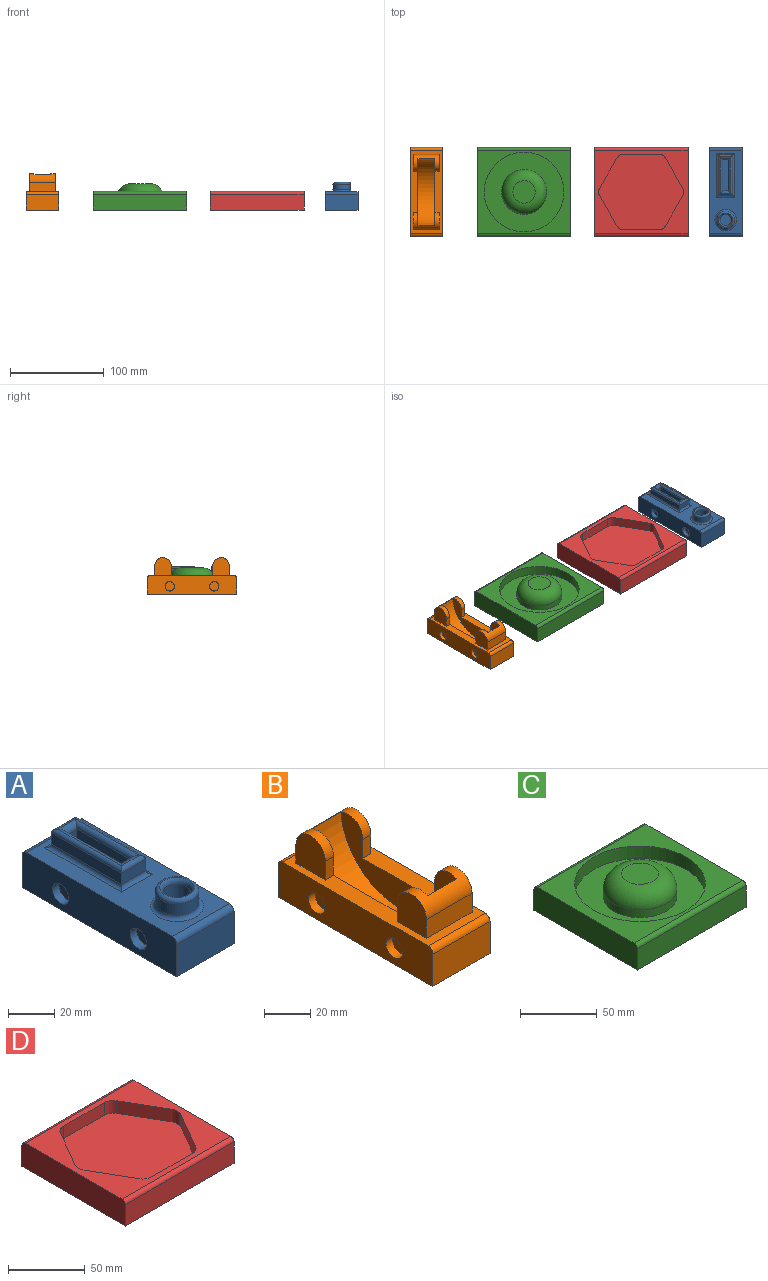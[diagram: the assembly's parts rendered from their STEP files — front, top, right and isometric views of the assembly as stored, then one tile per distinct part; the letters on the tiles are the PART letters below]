
ASSEMBLY  parts=4 mates=3
PART A: 43 faces, bbox 35x95x30.4 mm
  f0: plane 95x20mm, normal (-1,0,0), area 1732.7mm2, adj f2,f3,f4,f5,f18,f19,f39,f41
  f1: plane 95x20mm, normal (1,0,0), area 1732.7mm2, adj f2,f3,f4,f5,f18,f19,f35,f37
  f2: plane 89x35mm, normal (0,0,1), area 1806.5mm2, adj f0,f1,f18,f19,f30,f31,f32,f33
  f3: plane 35x17mm, normal (0,-1,0), area 595mm2, adj f0,f1,f5,f18
  f4: plane 35x17mm, normal (0,1,0), area 595mm2, adj f0,f1,f5,f19
  f5: plane 95x35mm, normal (0,0,-1), area 3325mm2, adj f0,f1,f3,f4
  f6: plane 33.08x17.5mm, normal (-1,0,0), area 577.5mm2, adj f7,f13,f17,f26,f28,f29
  f7: plane 17x6mm, normal (0,1,0), area 102mm2, adj f6,f8,f17,f28
  f8: plane 33.08x17.5mm, normal (1,0,0), area 577.5mm2, adj f7,f13,f17,f25,f28,f29
  f9: plane 15x6mm, normal (0,-1,0), area 90mm2, adj f10,f12,f23,f33
  f10: plane 43x6mm, normal (1,0,0), area 258mm2, adj f9,f11,f24,f34
  f11: plane 15x6mm, normal (0,1,0), area 90mm2, adj f10,f12,f22,f32
  f12: plane 43x6mm, normal (-1,0,0), area 258mm2, adj f9,f11,f21,f31
  f13: plane 17x6mm, normal (0,-1,0), area 102mm2, adj f6,f8,f17,f29
  f14: cylinder r=6mm len=17.4mm, axis (0,0,-1), area 656mm2, adj f16,f27
  f15: cylinder r=9.5mm len=19mm, axis (0,0,-1), area 358.1mm2, adj f20,f30
  f16: plane 12x12mm, normal (0,0,1), area 113.1mm2, adj f14
  f17: plane 33x6mm, normal (0,0,1), area 198mm2, adj f6,f7,f8,f13
  f18: cylinder r=3mm len=35mm, axis (-1,0,0), area 164.9mm2, adj f0,f1,f2,f3
  f19: cylinder r=3mm len=35mm, axis (1,0,0), area 164.9mm2, adj f0,f1,f2,f4
  f20: torus R=7.5mm, axis (0,0,1), area 173.2mm2, adj f15,f27
  f21: cylinder r=2mm len=43mm, axis (0,1,0), area 130.5mm2, adj f12,f22,f23,f25
  f22: cylinder r=2mm len=15mm, axis (1,0,0), area 42.6mm2, adj f11,f21,f24,f29
  f23: cylinder r=2mm len=15mm, axis (-1,0,0), area 42.6mm2, adj f9,f21,f24,f28
  f24: cylinder r=2mm len=43mm, axis (0,-1,0), area 130.5mm2, adj f10,f22,f23,f26
  f25: cylinder r=2.5mm len=39mm, axis (0,-1,0), area 139mm2, adj f8,f21,f28,f29
  f26: cylinder r=2.5mm len=39mm, axis (0,1,0), area 139mm2, adj f6,f24,f28,f29
  f27: torus R=9mm, axis (0,0,1), area 128.7mm2, adj f14,f20
  f28: cylinder r=3mm len=11mm, axis (1,0,0), area 36mm2, adj f6,f7,f8,f23,f25,f26
  f29: cylinder r=3mm len=11mm, axis (-1,0,0), area 36mm2, adj f6,f8,f13,f22,f25,f26
  f30: torus R=11.5mm, axis (0,0,1), area 201.9mm2, adj f2,f15
  f31: cylinder r=2mm len=47mm, axis (0,-1,0), area 139.7mm2, adj f2,f12,f32,f33
  f32: cylinder r=2mm len=19mm, axis (-1,0,0), area 51.7mm2, adj f2,f11,f31,f34
  f33: cylinder r=2mm len=19mm, axis (1,0,0), area 51.7mm2, adj f2,f9,f31,f34
  f34: cylinder r=2mm len=47mm, axis (0,1,0), area 139.7mm2, adj f2,f10,f32,f33
  f35: cylinder r=5.1mm len=10.2mm, axis (1,0,0), area 131.4mm2, adj f1,f36
  f36: plane 10.2x10.2mm, normal (1,0,0), area 81.7mm2, adj f35
  f37: cylinder r=5.1mm len=10.2mm, axis (1,0,0), area 131.4mm2, adj f1,f38
  f38: plane 10.2x10.2mm, normal (1,0,0), area 81.7mm2, adj f37
  f39: cylinder r=5.1mm len=10.2mm, axis (-1,0,0), area 131.4mm2, adj f0,f40
  f40: plane 10.2x10.2mm, normal (-1,0,0), area 81.7mm2, adj f39
  f41: cylinder r=5.1mm len=10.2mm, axis (-1,0,0), area 131.4mm2, adj f0,f42
  f42: plane 10.2x10.2mm, normal (-1,0,0), area 81.7mm2, adj f41
PART B: 31 faces, bbox 35x95x39 mm
  f0: plane 95x20mm, normal (-1,0,0), area 1735.9mm2, adj f2,f7,f8,f9,f21,f22,f27,f29
  f1: plane 95x20mm, normal (1,0,0), area 1735.9mm2, adj f2,f7,f8,f9,f21,f22,f23,f25
  f2: plane 89x35mm, normal (0,0,1), area 1315mm2, adj f0,f1,f3,f4,f10,f11,f12,f13
  f3: plane 10x5mm, normal (0,-1,0), area 50mm2, adj f2,f5,f11,f19
  f4: plane 10x5mm, normal (0,1,0), area 50mm2, adj f2,f6,f16,f19
  f5: cylinder r=9mm len=28mm, axis (1,0,0), area 454.4mm2, adj f3,f10,f11,f12,f13,f18,f19,f20
  f6: cylinder r=9mm len=28mm, axis (1,0,0), area 454.4mm2, adj f4,f14,f15,f16,f17,f18,f19,f20
  f7: plane 35x17mm, normal (0,-1,0), area 595mm2, adj f0,f1,f9,f22
  f8: plane 35x17mm, normal (0,1,0), area 595mm2, adj f0,f1,f9,f21
  f9: plane 95x35mm, normal (0,0,-1), area 3325mm2, adj f0,f1,f7,f8
  f10: plane 28x10mm, normal (0,1,0), area 280mm2, adj f2,f5,f11,f13
  f11: plane 19x18mm, normal (-1,0,0), area 307.2mm2, adj f2,f3,f5,f10
  f12: plane 10x5mm, normal (0,-1,0), area 50mm2, adj f2,f5,f13,f20
  f13: plane 19x18mm, normal (1,0,0), area 307.2mm2, adj f2,f5,f10,f12
  f14: plane 19x18mm, normal (1,0,0), area 307.2mm2, adj f2,f6,f15,f17
  f15: plane 10x5mm, normal (0,1,0), area 50mm2, adj f2,f6,f14,f20
  f16: plane 19x18mm, normal (-1,0,0), area 307.2mm2, adj f2,f4,f6,f17
  f17: plane 28x10mm, normal (0,-1,0), area 280mm2, adj f2,f6,f14,f16
  f18: cylinder r=35.5mm len=70.8mm, axis (1,0,0), area 1912mm2, adj f5,f6,f19,f20
  f19: plane 70.8x34mm, normal (1,0,0), area 999mm2, adj f2,f3,f4,f5,f6,f18
  f20: plane 70.8x34mm, normal (-1,0,0), area 999mm2, adj f2,f5,f6,f12,f15,f18
  f21: cylinder r=3mm len=35mm, axis (1,0,0), area 164.9mm2, adj f0,f1,f2,f8
  f22: cylinder r=3mm len=35mm, axis (-1,0,0), area 164.9mm2, adj f0,f1,f2,f7
  f23: cylinder r=5.05mm len=10.1mm, axis (1,0,0), area 130.1mm2, adj f1,f24
  f24: plane 10.1x10.1mm, normal (1,0,0), area 80.1mm2, adj f23
  f25: cylinder r=5.05mm len=10.1mm, axis (1,0,0), area 130.1mm2, adj f1,f26
  f26: plane 10.1x10.1mm, normal (1,0,0), area 80.1mm2, adj f25
  f27: cylinder r=5.05mm len=10.1mm, axis (-1,0,0), area 130.1mm2, adj f0,f28
  f28: plane 10.1x10.1mm, normal (-1,0,0), area 80.1mm2, adj f27
  f29: cylinder r=5.05mm len=10.1mm, axis (-1,0,0), area 130.1mm2, adj f0,f30
  f30: plane 10.1x10.1mm, normal (-1,0,0), area 80.1mm2, adj f29
PART C: 13 faces, bbox 100x95x28 mm
  f0: plane 95x20mm, normal (-1,0,0), area 1896.1mm2, adj f1,f3,f4,f5,f11,f12
  f1: plane 100x17mm, normal (0,-1,0), area 1700mm2, adj f0,f2,f5,f11
  f2: plane 95x20mm, normal (1,0,0), area 1896.1mm2, adj f1,f3,f4,f5,f11,f12
  f3: plane 100x17mm, normal (0,1,0), area 1700mm2, adj f0,f2,f5,f12
  f4: plane 100x89mm, normal (0,0,1), area 3225.5mm2, adj f0,f2,f7,f11,f12
  f5: plane 100x95mm, normal (0,0,-1), area 9500mm2, adj f0,f1,f2,f3
  f6: cylinder r=24mm len=48mm, axis (0,0,1), area 904.8mm2, adj f8,f10
  f7: cylinder r=42.5mm len=85mm, axis (0,0,1), area 2670.4mm2, adj f4,f8
  f8: plane 85x85mm, normal (0,0,1), area 3864.9mm2, adj f6,f7
  f9: plane 24x24mm, normal (0,0,1), area 452.4mm2, adj f10
  f10: torus R=12mm, axis (0,0,1), area 2326mm2, adj f6,f9
  f11: cylinder r=3mm len=100mm, axis (-1,0,0), area 471.2mm2, adj f0,f1,f2,f4
  f12: cylinder r=3mm len=100mm, axis (1,0,0), area 471.2mm2, adj f0,f2,f3,f4
PART D: 21 faces, bbox 100x95x20 mm
  f0: plane 100x89mm, normal (0,0,1), area 3238.6mm2, adj f2,f4,f6,f7,f8,f9,f10,f11
  f1: plane 100x17mm, normal (0,-1,0), area 1700mm2, adj f2,f4,f5,f20
  f2: plane 95x20mm, normal (1,0,0), area 1896.1mm2, adj f0,f1,f3,f5,f19,f20
  f3: plane 100x17mm, normal (0,1,0), area 1700mm2, adj f2,f4,f5,f19
  f4: plane 95x20mm, normal (-1,0,0), area 1896.1mm2, adj f0,f1,f3,f5,f19,f20
  f5: plane 100x95mm, normal (0,0,-1), area 9500mm2, adj f1,f2,f3,f4
  f6: cylinder r=8mm len=10mm, axis (0,0,1), area 83.8mm2, adj f0,f7,f17,f18
  f7: plane 32.5x18.76mm, normal (-0.87,-0.5,0), area 375.3mm2, adj f0,f6,f8,f18
  f8: cylinder r=8mm len=10mm, axis (0,0,1), area 83.8mm2, adj f0,f7,f9,f18
  f9: plane 37.53x10mm, normal (0,-1,0), area 375.3mm2, adj f0,f8,f10,f18
  f10: cylinder r=8mm len=10mm, axis (0,0,1), area 83.8mm2, adj f0,f9,f11,f18
  f11: plane 32.5x18.76mm, normal (0.87,-0.5,0), area 375.3mm2, adj f0,f10,f12,f18
  f12: cylinder r=8mm len=10mm, axis (0,0,1), area 83.8mm2, adj f0,f11,f13,f18
  f13: plane 32.5x18.76mm, normal (0.87,0.5,0), area 375.3mm2, adj f0,f12,f14,f18
  f14: cylinder r=8mm len=10mm, axis (0,0,1), area 83.8mm2, adj f0,f13,f15,f18
  f15: plane 37.53x10mm, normal (0,1,0), area 375.3mm2, adj f0,f14,f16,f18
  f16: cylinder r=8mm len=10mm, axis (0,0,1), area 83.8mm2, adj f0,f15,f17,f18
  f17: plane 32.5x18.76mm, normal (-0.87,0.5,0), area 375.3mm2, adj f0,f6,f16,f18
  f18: plane 91.06x81mm, normal (0,0,1), area 5661.4mm2, adj f6,f7,f8,f9,f10,f11,f12,f13
  f19: cylinder r=3mm len=100mm, axis (1,0,0), area 471.2mm2, adj f0,f2,f3,f4
  f20: cylinder r=3mm len=100mm, axis (-1,0,0), area 471.2mm2, adj f0,f1,f2,f4
PLACE A t=(81.59,19.92,-11.45)mm
PLACE B t=(-237.77,19.92,-21.44)mm
PLACE C t=(-133.5,19.92,-11.3)mm
PLACE D t=(-8.5,19.92,-11.3)mm fixed
MATE slider C.f2 <-> D.f4  axis (1,0,0) through (-83.5,19.92,-11.32)mm
MATE slider C.f0 <-> B.f1  axis (-1,0,0) through (-183.5,19.92,-11.32)mm
MATE slider A.f0 <-> D.f2  axis (-1,0,0) through (64.09,19.92,-11.32)mm
